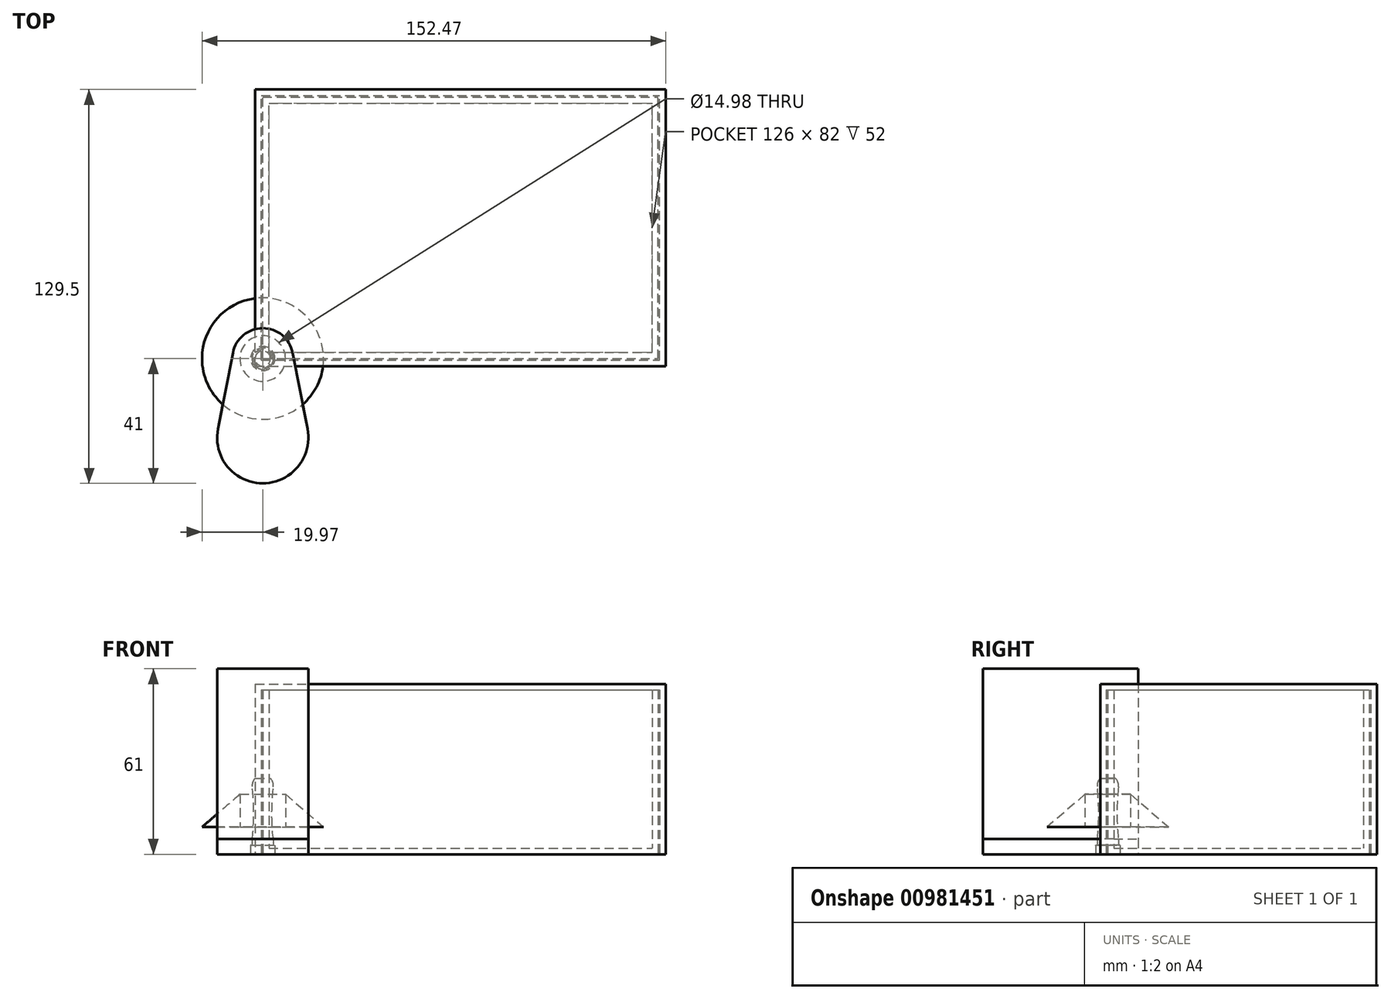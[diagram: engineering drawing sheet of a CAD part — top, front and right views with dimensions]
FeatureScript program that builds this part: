
annotation { "Feature Type Name" : "Feature", "Feature Type Description" : "" }
export const myFeature = defineFeature(function(context is Context, id is Id, definition is map)
    precondition{}
    {
        {
            var Q0;
            Q0=qCreatedBy(makeId("Top.planeOp"),FACE);
            var sketch = newSketch(context, id + "F0", { "sketchPlane" : qUnion([Q0])});
            skLineSegment(sketch, "E0.bottom", {"start": v(0, 0) * mm, "end": v(130, 0) * mm});
            skLineSegment(sketch, "E0.top", {"start": v(0, 86) * mm, "end": v(130, 86) * mm});
            skLineSegment(sketch, "E0.left", {"start": v(0, 0) * mm, "end": v(0, 86) * mm});
            skLineSegment(sketch, "E0.right", {"start": v(130, 0) * mm, "end": v(130, 86) * mm});
            skSolve(sketch);
        }
        {
            var Q0;
            Q0=makeQuery(id+"F0.imprint","IMPRINT",FACE,{"disambiguationData":[TD([[makeQuery(id+"F0.imprint","IMPRINT",EDGE,{"derivedFrom":sQuery(id+"F0.wireOp",EDGE,"E0.bottom")}),1.0]])]});
            extrude(context, id + "F1", {"entities" : qUnion([Q0]), "depth" : 54 * mm, "offsetDistance" : 25 * mm});
        }
        {
            var Q0;
            Q0=makeQuery(id+"F1.opExtrude","CAP_FACE",FACE,{"disambiguationData":[OSD([sQuery(id+"F0.wireOp",EDGE,"E0.bottom"),sQuery(id+"F0.wireOp",EDGE,"E0.top"),sQuery(id+"F0.wireOp",EDGE,"E0.left"),sQuery(id+"F0.wireOp",EDGE,"E0.right")])],"isStart":false});
            shell(context, id + "F2", {"entities" : qUnion([Q0]), "thickness" : 2 * mm});
        }
        {
            var Q0;
            Q0=qCreatedBy(makeId("Top.planeOp"),FACE);
            var sketch = newSketch(context, id + "F3", { "sketchPlane" : qUnion([Q0])});
            skLineSegment(sketch, "E1.bottom", {"start": v(-2.5, -2.5) * mm, "end": v(132.5, -2.5) * mm});
            skLineSegment(sketch, "E1.top", {"start": v(-2.5, 88.5) * mm, "end": v(132.5, 88.5) * mm});
            skLineSegment(sketch, "E1.left", {"start": v(-2.5, -2.5) * mm, "end": v(-2.5, 88.5) * mm});
            skLineSegment(sketch, "E1.right", {"start": v(132.5, -2.5) * mm, "end": v(132.5, 88.5) * mm});
            skSolve(sketch);
        }
        {
            var Q0;
            Q0=makeQuery(id+"F3.imprint","IMPRINT",FACE,{"disambiguationData":[TD([[makeQuery(id+"F3.imprint","IMPRINT",EDGE,{"derivedFrom":sQuery(id+"F3.wireOp",EDGE,"E1.bottom")}),1.0]])]});
            var Q1;
            Q1=makeQuery(id+"F1.opExtrude","CAP_FACE",FACE,{"disambiguationData":[OSD([sQuery(id+"F0.wireOp",EDGE,"E0.bottom"),sQuery(id+"F0.wireOp",EDGE,"E0.top"),sQuery(id+"F0.wireOp",EDGE,"E0.left"),sQuery(id+"F0.wireOp",EDGE,"E0.right")])],"isStart":false});
            extrude(context, id + "F4", {"entities" : qUnion([Q0]), "endBound" : BoundingType.UP_TO_SURFACE, "depth" : 26.3 * mm, "endBoundEntityFace" : qUnion([Q1]), "hasOffset" : true, "offsetDistance" : 2 * mm, "offsetOppositeDirection" : true});
        }
        {
            var Q0;
            Q0=makeQuery(id+"F4.opExtrude","CAP_FACE",FACE,{"disambiguationData":[OSD([sQuery(id+"F3.wireOp",EDGE,"E1.bottom"),sQuery(id+"F3.wireOp",EDGE,"E1.top"),sQuery(id+"F3.wireOp",EDGE,"E1.left"),sQuery(id+"F3.wireOp",EDGE,"E1.right")])],"isStart":true});
            shell(context, id + "F5", {"entities" : qUnion([Q0]), "thickness" : 2 * mm});
        }
        {
            var Q0;
            Q0=qCreatedBy(makeId("Top.planeOp"),FACE);
            var sketch = newSketch(context, id + "F6", { "sketchPlane" : qUnion([Q0])});
            skArc(sketch, "E2", {"start": v(9.81, 1.92) * mm, "mid": v(0, 10) * mm, "end": v(-9.81, 1.92) * mm});
            skArc(sketch, "E3", {"start": v(-14.72, -23.12) * mm, "mid": v(0, -41) * mm, "end": v(14.72, -23.12) * mm});
            skLineSegment(sketch, "E4", {"start": v(-9.81, 1.92) * mm, "end": v(-14.72, -23.12) * mm});
            skLineSegment(sketch, "E5", {"start": v(9.81, 1.92) * mm, "end": v(14.72, -23.12) * mm});
            skSolve(sketch);
        }
        {
            var Q0;
            Q0=makeQuery(id+"F6.imprint","IMPRINT",FACE,{"disambiguationData":[TD([[makeQuery(id+"F6.imprint","IMPRINT",EDGE,{"derivedFrom":sQuery(id+"F6.wireOp",EDGE,"E2")}),1.0]])]});
            extrude(context, id + "F7", {"entities" : qUnion([Q0]), "depth" : 5 * mm, "offsetDistance" : 25 * mm});
        }
        {
            var Q0;
            Q0=makeQuery(id+"F6.imprint","IMPRINT",FACE,{"disambiguationData":[TD([[makeQuery(id+"F6.imprint","IMPRINT",EDGE,{"derivedFrom":sQuery(id+"F6.wireOp",EDGE,"E2")}),1.0]])]});
            extrude(context, id + "F8", {"entities" : qUnion([Q0]), "depth" : 61 * mm, "offsetDistance" : 25 * mm, "hasSecondDirection" : true, "secondDirectionOppositeDirection" : false, "secondDirectionDepth" : 5 * mm});
        }
        {
            var Q0;
            Q0=qCreatedBy(makeId("Front.planeOp"),FACE);
            var sketch = newSketch(context, id + "F9", { "sketchPlane" : qUnion([Q0])});
            skLineSegment(sketch, "E6", {"start": v(0, 0) * mm, "end": v(0, 31.15) * mm});
            skArc(sketch, "E7", {"start": v(3.48, 22.17) * mm, "mid": v(3, 13.33) * mm, "end": v(3.5, 4.5) * mm});
            skArc(sketch, "E8", {"start": v(3.48, 22.17) * mm, "mid": v(3.3, 23.7) * mm, "end": v(2.5, 25) * mm});
            skLineSegment(sketch, "E9", {"start": v(3.5, 4.5) * mm, "end": v(3.5, 3) * mm});
            skLineSegment(sketch, "E10", {"start": v(3.5, 3) * mm, "end": v(4, 3) * mm});
            skLineSegment(sketch, "E11", {"start": v(4, 3) * mm, "end": v(4, 0) * mm});
            skLineSegment(sketch, "E12", {"start": v(4, 0) * mm, "end": v(0, 0) * mm});
            skLineSegment(sketch, "E13", {"start": v(0, 25) * mm, "end": v(2.5, 25) * mm});
            skLineSegment(sketch, "E14", {"start": v(-19.97, 8.93) * mm, "end": v(-7.49, 8.93) * mm});
            skLineSegment(sketch, "E15", {"start": v(-7.49, 8.93) * mm, "end": v(-7.49, 19.73) * mm});
            skLineSegment(sketch, "E16", {"start": v(-7.49, 19.73) * mm, "end": v(-19.97, 8.93) * mm});
            skSolve(sketch);
        }
        {
            var Q0;
            Q0=makeQuery(id+"F9.imprint","IMPRINT",FACE,{"disambiguationData":[TD([[makeQuery(id+"F9.imprint","IMPRINT",EDGE,{"derivedFrom":sQuery(id+"F9.wireOp",EDGE,"E7")}),-1.0]])]});
            var Q1;
            Q1=sQuery(id+"F9.wireOp",EDGE,"E6");
            revolve(context, id + "F10", {"surfaceOperationType" : NewSurfaceOperationType.NEW, "entities" : qUnion([Q0]), "axis" : qUnion([Q1]), "revolveType" : RevolveType.FULL});
        }
        {
            var Q0;
            Q0=makeQuery(id+"F10.opRevolve","SWEPT_EDGE",EDGE,{"disambiguationData":[OSD([sQuery(id+"F9.wireOp",EDGE,"E7"),sQuery(id+"F9.wireOp",EDGE,"E9")])]});
            fillet(context, id + "F11", {"entities" : qUnion([Q0]), "radius" : 5 * mm, "tangentPropagation" : true, "allowEdgeOverflow" : false});
        }
        {
            var Q0;
            Q0=makeQuery(id+"F10.opRevolve","SWEPT_EDGE",EDGE,{"disambiguationData":[OSD([sQuery(id+"F9.wireOp",EDGE,"E9"),sQuery(id+"F9.wireOp",EDGE,"E10")])]});
            var Q1;
            Q1=makeQuery(id+"F10.opRevolve","SWEPT_EDGE",EDGE,{"disambiguationData":[OSD([sQuery(id+"F9.wireOp",EDGE,"E10"),sQuery(id+"F9.wireOp",EDGE,"E11")])]});
            fillet(context, id + "F12", {"entities" : qUnion([Q0, Q1]), "radius" : 0.1 * mm, "tangentPropagation" : true, "allowEdgeOverflow" : false});
        }
        {
            var Q0;
            Q0=makeQuery(id+"F9.imprint","IMPRINT",FACE,{"disambiguationData":[TD([[makeQuery(id+"F9.imprint","IMPRINT",EDGE,{"derivedFrom":sQuery(id+"F9.wireOp",EDGE,"E14")}),1.0]])]});
            var Q1;
            Q1=sQuery(id+"F9.wireOp",EDGE,"E6");
            revolve(context, id + "F13", {"surfaceOperationType" : NewSurfaceOperationType.NEW, "entities" : qUnion([Q0]), "axis" : qUnion([Q1]), "revolveType" : RevolveType.FULL});
        }
    });
